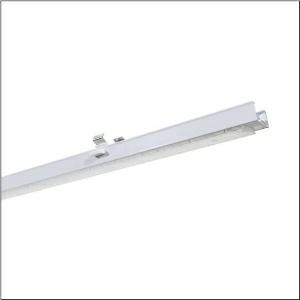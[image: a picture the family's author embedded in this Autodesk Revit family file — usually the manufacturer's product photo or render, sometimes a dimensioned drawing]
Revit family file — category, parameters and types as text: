
# Revit family: trunking_flex_31_51re19mb4cb
name_source: partatom
category: Lighting Fixtures
units: mm (PartAtom-declared; Revit-internal decimal feet)

## family parameters
Cut with Voids When Loaded = No
Host = Face
Light Source = No
Part Type = Normal
Room Calculation Point = No
Round Connector Dimension = Use Diameter
Shared = No

## types (1)
- --- (1 x LED, 11500 lm, 66 W, 4000K)
    Apparent Load = 66 VA
    CIE Flux Codes = 66 89 98 99 100
    Color Rendering = 80
    Color Temperature = 4000K
    Default Elevation = 1800 mm
    Description = Trunking Flex 31, luminaire insert, of extruded aluminium section, coated, traffic white (RAL 9016), length: 1.472mm, width: 91mm, height: 53mm, LED rated luminous flux: 11.500lm, light colour: 840, control gear: ON/OFF Multilumen, with system connector: socket, mains connection: 220..240V, AC, 50/60Hz, rated input power: 66W, connected load according to luminous flux setting (19/24/32/37/47/52/60/66W), luminous flux adjustable on luminaire in eight steps (3450/4380/5800/6700/8350/9200/10500/11500lm ), primary light control with lens, of plastic, primary optical cover: cover, of PMMA, light emission: direct distribution, primary light characteristic: double asymmetric, protection rating (complete): IP20, insulation class (complete): insulation class I (protective earthing), certification: CE, UKCA, impact resistance: IK02, permissible ambient temperature for indoor applications: -20..+40°C, packaging unit: 1 piece
    Height = 58 mm
    Lamp = 1 x LED
    Lamp Light Flux = 11500 lm
    Lamp Power = 66 W
    Lamp count = 1
    Length = 1472 mm
    Luminous efficacy = 174 lm/W
    Manufacturer = Siteco
    ModVariant = No
    Model = 51RE19MB4CB
    Mounting Place = Ceiling
    Mounting Type = Pendant
    Number of Poles = 1
    OnlyDefault = Yes
    Power Factor = 1
    Product Name = Trunking Flex 31
    Product group = luminaire insert
    ProductGroupID = 902
    Protection Class = Protection class I
    Protection Degree = IP 20
    RLX_Detail_Level = 1
    RLX_Emergency_Light_Flux = 0 lm
    RLX_Emergency_Type = 0
    RLX_Emergency_Type_DB = No
    RlxData = <blob elided: 21141 chars, md5=19aeaeb8>
    Socket = socket
    Standby Power = 0 W
    System Light Flux = 11500 lm
    System Power = 66 W
    Type Comments = factory setting: luminous flux: 100 % | (ON | ON | ON)
    Type Image = l_1266702.jpg
    URL = http://relux.com
    VarID = @adj_059210
    Voltage = 0 V
    Weight = 0.00 kg
    Width = 65 mm

## geometry (parser evidence)
native form markers: Blend x4, Sweep x11
no freeform markers — native parametric forms only
